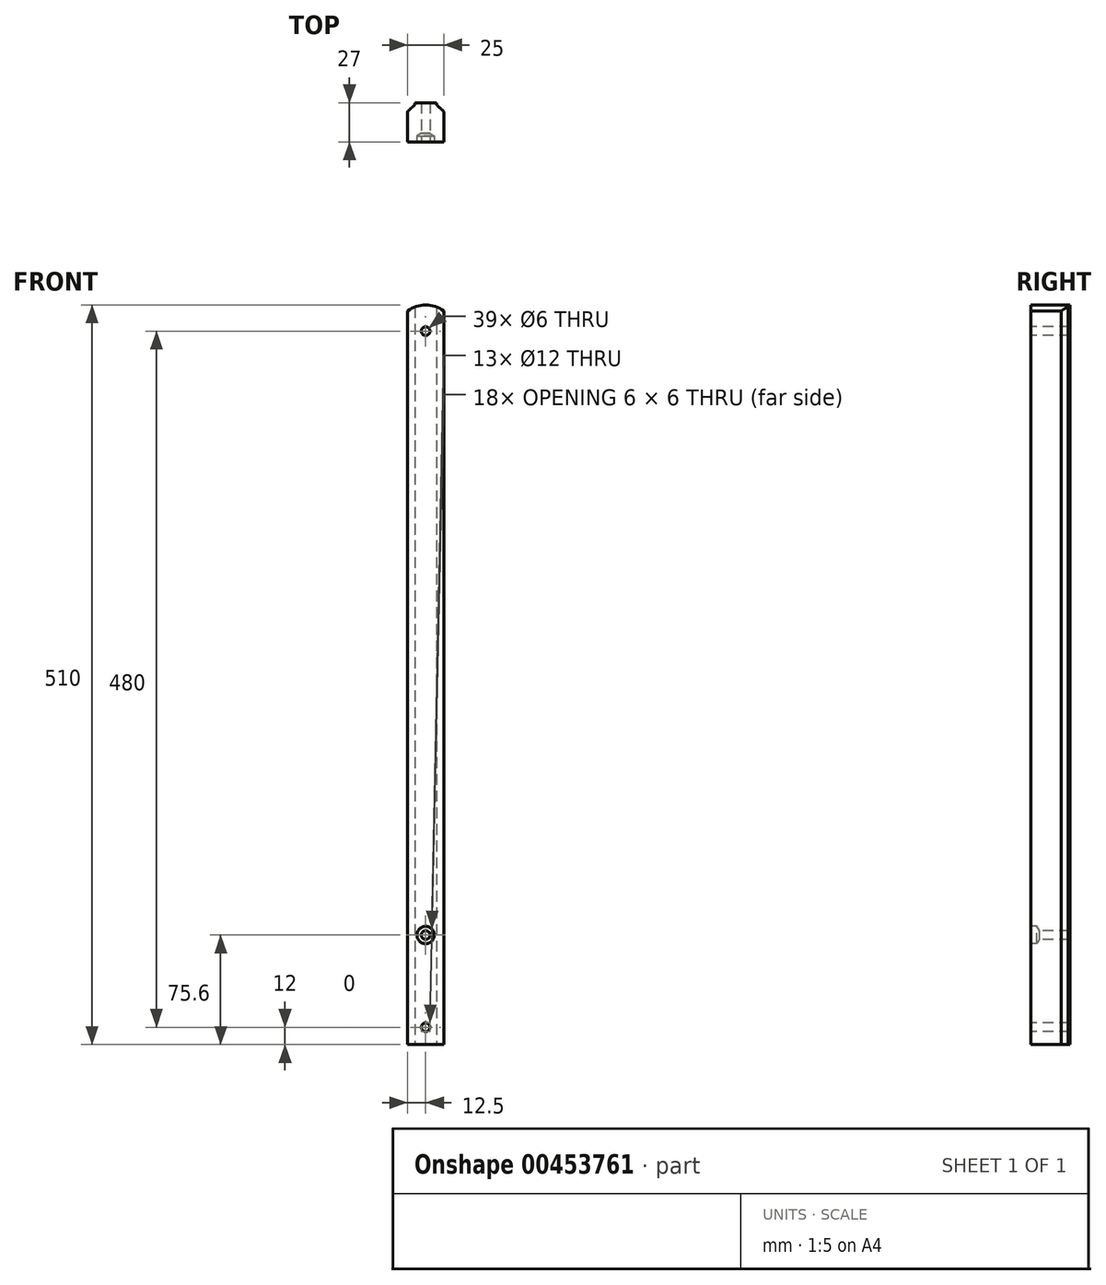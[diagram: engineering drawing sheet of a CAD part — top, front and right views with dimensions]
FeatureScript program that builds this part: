
annotation { "Feature Type Name" : "Feature", "Feature Type Description" : "" }
export const myFeature = defineFeature(function(context is Context, id is Id, definition is map)
    precondition{}
    {
        {
            var Q0;
            Q0=qCreatedBy(makeId("Top.planeOp"),FACE);
            var sketch = newSketch(context, id + "F0", { "sketchPlane" : qUnion([Q0])});
            skLineSegment(sketch, "E0.bottom", {"start": v(0, 0) * mm, "end": v(-25, 0) * mm});
            skLineSegment(sketch, "E0.left", {"start": v(0, 0) * mm, "end": v(0, 21) * mm});
            skLineSegment(sketch, "E0.right", {"start": v(-25, 0) * mm, "end": v(-25, 21) * mm});
            skLineSegment(sketch, "E1", {"start": v(-12.5, 27) * mm, "end": v(-12.5, 0) * mm, "construction": true});
            skLineSegment(sketch, "E2", {"start": v(-25, 21) * mm, "end": v(-20, 25.5) * mm});
            skLineSegment(sketch, "E3", {"start": v(0, 21) * mm, "end": v(-5, 25.5) * mm});
            skLineSegment(sketch, "E4", {"start": v(-20, 25.5) * mm, "end": v(-20, 27) * mm});
            skLineSegment(sketch, "E5", {"start": v(-5, 25.5) * mm, "end": v(-5, 27) * mm});
            skLineSegment(sketch, "E6", {"start": v(-20, 27) * mm, "end": v(-5, 27) * mm});
            skPoint(sketch, "E7.visualSharp", {"position": v(0, 0) * mm});
            skSolve(sketch);
        }
        {
            var Q0;
            Q0=makeQuery(id+"F0.imprint","IMPRINT",FACE,{"disambiguationData":[TD([[makeQuery(id+"F0.imprint","IMPRINT",EDGE,{"derivedFrom":sQuery(id+"F0.wireOp",EDGE,"E0.bottom")}),-1.0]])]});
            extrude(context, id + "F1", {"entities" : qUnion([Q0]), "depth" : 510 * mm});
        }
        {
            var Q0;
            Q0=makeQuery(id+"F1.opExtrude","SWEPT_FACE",FACE,{"disambiguationData":[OSD([sQuery(id+"F0.wireOp",EDGE,"E0.bottom")])]});
            var sketch = newSketch(context, id + "F2", { "sketchPlane" : qUnion([Q0])});
            skLineSegment(sketch, "E8.left", {"start": v(0, 0) * mm, "end": v(0, 0) * mm});
            skLineSegment(sketch, "E8.right", {"start": v(-25, 0) * mm, "end": v(-25, 0) * mm});
            skArc(sketch, "E9", {"start": v(-12.5, 510) * mm, "mid": v(-19.06, 508.98) * mm, "end": v(-25, 506) * mm});
            skArc(sketch, "E10.trimOffspring", {"start": v(0, 506) * mm, "mid": v(-5.94, 508.98) * mm, "end": v(-12.5, 510) * mm});
            skLineSegment(sketch, "E11", {"start": v(-25, 506) * mm, "end": v(-25, 510) * mm});
            skLineSegment(sketch, "E12", {"start": v(-25, 510) * mm, "end": v(0, 510) * mm});
            skLineSegment(sketch, "E13", {"start": v(0, 510) * mm, "end": v(0, 506) * mm});
            skSolve(sketch);
        }
        {
            var Q0;
            {var subQ0=sQuery(id+"F2.wireOp",EDGE,"E9");Q0=makeQuery(id+"F2.imprint","IMPRINT",FACE,{"disambiguationData":[TD([[makeQuery(id+"F2.imprint","IMPRINT",EDGE,{"derivedFrom":subQ0}),-1.0]])]});}
            var Q1;
            {var subQ0=sQuery(id+"F2.wireOp",EDGE,"E10.trimOffspring");Q1=makeQuery(id+"F2.imprint","IMPRINT",FACE,{"disambiguationData":[TD([[makeQuery(id+"F2.imprint","IMPRINT",EDGE,{"derivedFrom":subQ0}),-1.0]])]});}
            var Q2;
            Q2=sQuery(id+"F2.wireOp",EDGE,"E11");
            var Q3;
            Q3=sQuery(id+"F2.wireOp",EDGE,"E9");
            var Q4;
            Q4=sQuery(id+"F2.wireOp",EDGE,"E10.trimOffspring");
            var Q5;
            Q5=sQuery(id+"F2.wireOp",EDGE,"E12");
            var Q6;
            Q6=sQuery(id+"F2.wireOp",EDGE,"E13");
            extrude(context, id + "F3", {"entities" : qUnion([Q0, Q1]), "operationType" : NewBodyOperationType.REMOVE, "surfaceEntities" : qUnion([Q2, Q3, Q4, Q5, Q6]), "oppositeDirection" : true, "depth" : 27 * mm});
        }
        {
            var Q0;
            Q0=makeQuery(id+"F1.opExtrude","SWEPT_FACE",FACE,{"disambiguationData":[OSD([sQuery(id+"F0.wireOp",EDGE,"E0.bottom")])]});
            var sketch = newSketch(context, id + "F4", { "sketchPlane" : qUnion([Q0])});
            skLineSegment(sketch, "E14", {"start": v(-25, 506) * mm, "end": v(-25, 0) * mm, "construction": true});
            skLineSegment(sketch, "E15", {"start": v(-25, 0) * mm, "end": v(0, 0) * mm, "construction": true});
            skLineSegment(sketch, "E16", {"start": v(0, 0) * mm, "end": v(0, 506) * mm, "construction": true});
            skLineSegment(sketch, "E17", {"start": v(0, 506) * mm, "end": v(-25, 506) * mm, "construction": true});
            skCircle(sketch, "E18", {"center": v(-12.5, 12) * mm, "radius": 3 * mm});
            skPoint(sketch, "E18.centerSnap0", {"position": v(-12.5, 0) * mm});
            skCircle(sketch, "E19", {"center": v(-12.5, 75.6) * mm, "radius": 3 * mm});
            skCircle(sketch, "E20", {"center": v(-12.5, 492) * mm, "radius": 3 * mm});
            skSolve(sketch);
        }
        {
            var Q0;
            Q0=sQuery(id+"F4.wireOp",VERTEX,"E20.center");
            var Q1;
            Q1=sQuery(id+"F4.wireOp",VERTEX,"E18.center");
            var Q2;
            Q2=sQuery(id+"F4.wireOp",VERTEX,"E19.center");
            var Q3;
            Q3=makeQuery(id+"F1.opExtrude","SWEPT_BODY",BODY,{"disambiguationData":[OSD([sQuery(id+"F0.wireOp",EDGE,"E0.bottom"),sQuery(id+"F0.wireOp",EDGE,"E0.left"),sQuery(id+"F0.wireOp",EDGE,"E0.right"),sQuery(id+"F0.wireOp",EDGE,"E2"),sQuery(id+"F0.wireOp",EDGE,"E3"),sQuery(id+"F0.wireOp",EDGE,"E4"),sQuery(id+"F0.wireOp",EDGE,"E5"),sQuery(id+"F0.wireOp",EDGE,"E6")])]});
            hole(context, id + "F5", {"style" : HoleStyle.SIMPLE, "endStyle" : HoleEndStyle.THROUGH, "holeDiameter" : 6 * mm, "isTappedThrough" : true, "tappedDepth" : 12 * mm, "tapClearance" : 3, "locations" : qUnion([Q0, Q1, Q2]), "scope" : qUnion([Q3])});
        }
        {
            var Q0;
            Q0=makeQuery(id+"F1.opExtrude","SWEPT_FACE",FACE,{"disambiguationData":[OSD([sQuery(id+"F0.wireOp",EDGE,"E0.bottom")])]});
            var sketch = newSketch(context, id + "F6", { "sketchPlane" : qUnion([Q0])});
            skCircle(sketch, "E21", {"center": v(-12.5, 75.6) * mm, "radius": 6 * mm});
            skSolve(sketch);
        }
        {
            var Q0;
            Q0=sQuery(id+"F6.wireOp",VERTEX,"E21.center");
            var Q1;
            Q1=makeQuery(id+"F1.opExtrude","SWEPT_BODY",BODY,{"disambiguationData":[OSD([sQuery(id+"F0.wireOp",EDGE,"E0.bottom"),sQuery(id+"F0.wireOp",EDGE,"E0.left"),sQuery(id+"F0.wireOp",EDGE,"E0.right"),sQuery(id+"F0.wireOp",EDGE,"E2"),sQuery(id+"F0.wireOp",EDGE,"E3"),sQuery(id+"F0.wireOp",EDGE,"E4"),sQuery(id+"F0.wireOp",EDGE,"E5"),sQuery(id+"F0.wireOp",EDGE,"E6")])]});
            hole(context, id + "F7", {"style" : HoleStyle.SIMPLE, "endStyle" : HoleEndStyle.BLIND, "holeDiameter" : 12 * mm, "holeDepth" : 4 * mm, "isTappedThrough" : true, "tappedDepth" : 12 * mm, "tapClearance" : 3, "locations" : qUnion([Q0]), "scope" : qUnion([Q1])});
        }
    });
